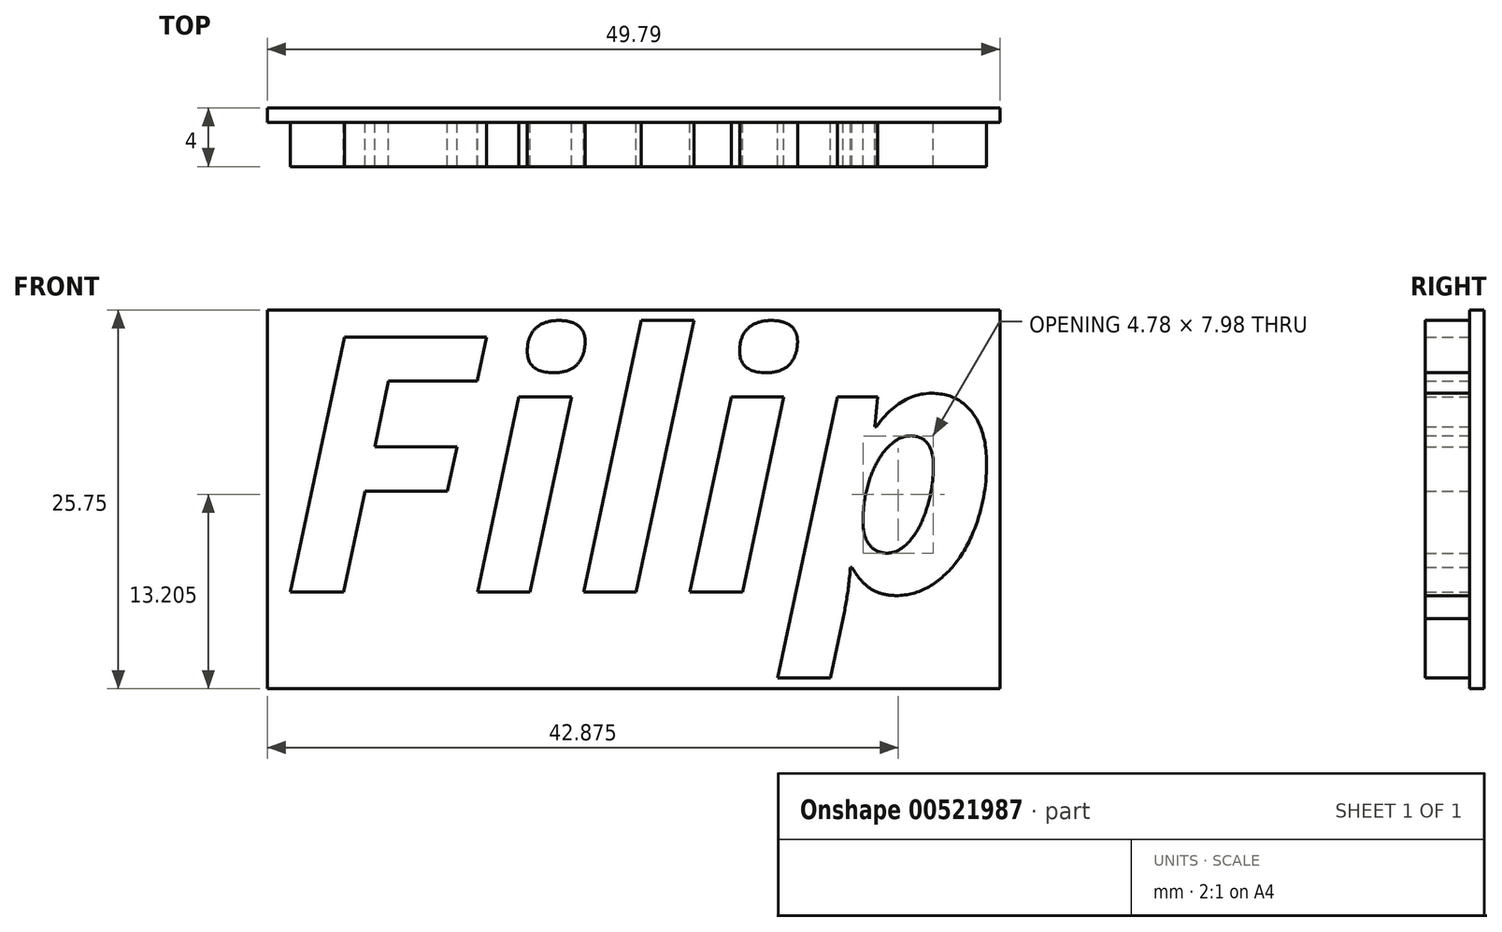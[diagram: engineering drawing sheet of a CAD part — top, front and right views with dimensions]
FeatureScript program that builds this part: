
annotation { "Feature Type Name" : "Feature", "Feature Type Description" : "" }
export const myFeature = defineFeature(function(context is Context, id is Id, definition is map)
    precondition{}
    {
        {
            var Q0;
            Q0=qCreatedBy(makeId("Front.planeOp"),FACE);
            var sketch = newSketch(context, id + "F0", { "sketchPlane" : qUnion([Q0])});
            skText(sketch, "E0", { "text": "Filip", "fontName": "OpenSans-BoldItalic.ttf"});
            const initialGuessF0  = {"E0": [-0.04475, -0.00012, 1, 0, 0.0175]};
            skSetInitialGuess(sketch, initialGuessF0);
            skSolve(sketch);
        }
        {
            var Q0;
            Q0=qSketchRegion(id+"F0",true);
            extrude(context, id + "F1", {"entities" : qUnion([Q0]), "depth" : 3 * mm});
        }
        {
            var Q0;
            Q0=makeQuery(id+"F0.imprint","IMPRINT",FACE,{"disambiguationData":[TD([[makeQuery(id+"F0.imprint","IMPRINT",EDGE,{"derivedFrom":sQuery(id+"F0.wireOp",EDGE,"E0.sketch_text.stroke-36")}),-1.0]])]});
            var sketch = newSketch(context, id + "F2", { "sketchPlane" : qUnion([Q0])});
            skLineSegment(sketch, "E1.bottom", {"start": v(-45.7, 19.06) * mm, "end": v(4.1, 19.06) * mm});
            skLineSegment(sketch, "E1.top", {"start": v(-45.7, -6.7) * mm, "end": v(4.1, -6.7) * mm});
            skLineSegment(sketch, "E1.left", {"start": v(-45.7, 19.06) * mm, "end": v(-45.7, -6.7) * mm});
            skLineSegment(sketch, "E1.right", {"start": v(4.1, 19.06) * mm, "end": v(4.1, -6.7) * mm});
            skSolve(sketch);
        }
        {
            var Q0;
            Q0 = qSketchRegion(id + "F2", true);
            extrude(context, id + "F3", {"entities" : qUnion([Q0]), "oppositeDirection" : true, "depth" : 1 * mm, "offsetDistance" : 25 * mm});
        }
    });
